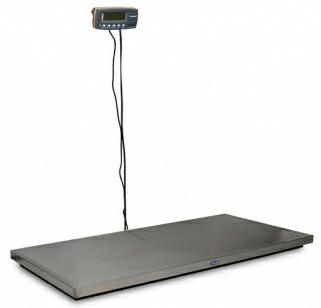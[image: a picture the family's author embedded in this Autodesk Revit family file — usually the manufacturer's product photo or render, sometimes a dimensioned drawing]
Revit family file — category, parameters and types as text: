
# Revit family: Midmark - Platform Scale
name_source: partatom
category: Specialty Equipment
revit_build: Autodesk Revit 2017 (Build: 20190507_1515(x64)
units: mm (PartAtom-declared; Revit-internal decimal feet)

## family parameters
Always vertical = Yes
Cut with Voids When Loaded = No
OmniClass Number = 23.25.61.00
Part Type = Normal
Room Calculation Point = No
Round Connector Dimension = Use Diameter
Shared = No
Work Plane-Based = No

## types (1)
- Post Mount Readout with No Slip Mat
    Depth = 1' - 10"
    Description = Recessing this scale is not Recommended.
    Manufacturer = MIDMARK
    Model = 110-3110-00
    No Slip Mat Material = Rubber, Black
    Platform Surface Material = Stainless Steel, Polished
    Post & Frame Material = Steel, Paint Finish, Black, Matte
    Readout Frame Material = Stainless Steel, Polished
    Readout Width = 0' - 6 3/4"
    Scale Display Material = Plastic, Opaque White
    Scale Platform = 0' - 2 11/16"
    Type Comments = Platform Scale. 44"L x 22"W Stainless Steel with Post Mount readout and No Slip Mat Included.
    Type Image = 05-101A_Floor Scale_Wall Mnt.jpg
    Width = 3' - 8"

## geometry (parser evidence)
native form markers: Sweep x3
no freeform markers — native parametric forms only
